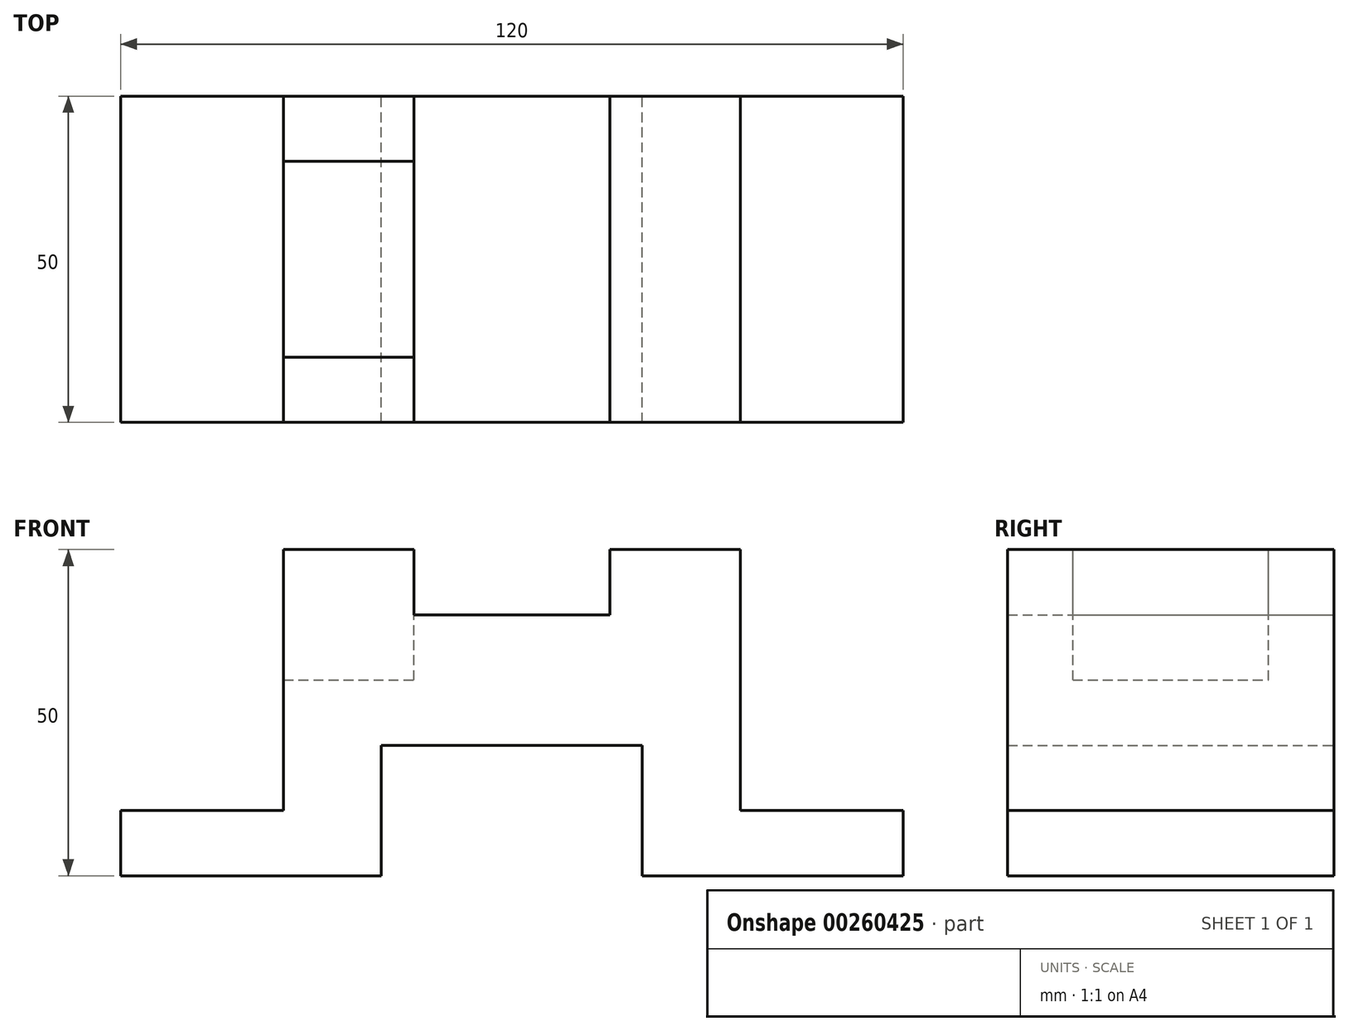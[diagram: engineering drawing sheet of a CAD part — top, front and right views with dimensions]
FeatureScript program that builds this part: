
annotation { "Feature Type Name" : "Feature", "Feature Type Description" : "" }
export const myFeature = defineFeature(function(context is Context, id is Id, definition is map)
    precondition{}
    {
        {
            var Q0;
            Q0=qCreatedBy(makeId("Front.planeOp"),FACE);
            var sketch = newSketch(context, id + "F0", { "sketchPlane" : qUnion([Q0])});
            skLineSegment(sketch, "E0", {"start": v(-40.34, 0) * mm, "end": v(-40.34, 10) * mm});
            skLineSegment(sketch, "E1", {"start": v(-40.34, 10) * mm, "end": v(-15.34, 10) * mm});
            skLineSegment(sketch, "E2", {"start": v(-15.34, 10) * mm, "end": v(-15.34, 50) * mm});
            skLineSegment(sketch, "E3", {"start": v(-15.34, 50) * mm, "end": v(4.66, 50) * mm});
            skLineSegment(sketch, "E4", {"start": v(4.66, 50) * mm, "end": v(4.66, 40) * mm});
            skLineSegment(sketch, "E5", {"start": v(4.66, 40) * mm, "end": v(34.66, 40) * mm});
            skLineSegment(sketch, "E6", {"start": v(34.66, 40) * mm, "end": v(34.66, 50) * mm});
            skLineSegment(sketch, "E7", {"start": v(34.66, 50) * mm, "end": v(54.66, 50) * mm});
            skLineSegment(sketch, "E8", {"start": v(54.66, 50) * mm, "end": v(54.66, 10) * mm});
            skLineSegment(sketch, "E9", {"start": v(54.66, 10) * mm, "end": v(79.66, 10) * mm});
            skLineSegment(sketch, "E10", {"start": v(79.66, 10) * mm, "end": v(79.66, 0) * mm});
            skLineSegment(sketch, "E11", {"start": v(79.66, 0) * mm, "end": v(39.66, 0) * mm});
            skLineSegment(sketch, "E12", {"start": v(39.66, 0) * mm, "end": v(39.66, 20) * mm});
            skLineSegment(sketch, "E13", {"start": v(39.66, 20) * mm, "end": v(-0.34, 20) * mm});
            skLineSegment(sketch, "E14", {"start": v(-0.34, 20) * mm, "end": v(-0.34, 0) * mm});
            skLineSegment(sketch, "E15", {"start": v(-0.34, 0) * mm, "end": v(-40.34, 0) * mm});
            skSolve(sketch);
        }
        {
            var Q0;
            Q0 = qSketchRegion(id + "F0", true);
            extrude(context, id + "F1", {"entities" : qUnion([Q0]), "depth" : 50 * mm});
        }
        {
            var Q0;
            Q0=makeQuery(id+"F1.opExtrude","SWEPT_FACE",FACE,{"disambiguationData":[OSD([sQuery(id+"F0.wireOp",EDGE,"E3")])]});
            var sketch = newSketch(context, id + "F2", { "sketchPlane" : qUnion([Q0])});
            skLineSegment(sketch, "E16.0", {"start": v(54.66, -50) * mm, "end": v(54.66, 0) * mm});
            skLineSegment(sketch, "E17.bottom", {"start": v(-15.34, -10) * mm, "end": v(54.66, -10) * mm});
            skLineSegment(sketch, "E17.top", {"start": v(-15.34, -40) * mm, "end": v(54.66, -40) * mm});
            skLineSegment(sketch, "E17.left", {"start": v(-15.34, -10) * mm, "end": v(-15.34, -40) * mm});
            skLineSegment(sketch, "E17.right", {"start": v(54.66, -10) * mm, "end": v(54.66, -40) * mm});
            skSolve(sketch);
        }
        {
            var Q0;
            {var subQ0=sQuery(id+"F2.wireOp",EDGE,"E17.left");Q0=makeQuery(id+"F2.imprint","IMPRINT",FACE,{"disambiguationData":[TD([[makeQuery(id+"F2.imprint","IMPRINT",EDGE,{"derivedFrom":subQ0}),-1.0]])]});}
            var Q1;
            {var subQ0=sQuery(id+"F2.wireOp",EDGE,"E17.right");Q1=makeQuery(id+"F2.imprint","IMPRINT",FACE,{"disambiguationData":[TD([[makeQuery(id+"F2.imprint","IMPRINT",EDGE,{"derivedFrom":subQ0}),-1.0]])]});}
            extrude(context, id + "F3", {"entities" : qUnion([Q0, Q1]), "operationType" : NewBodyOperationType.REMOVE, "oppositeDirection" : true, "depth" : 20 * mm});
        }
    });
